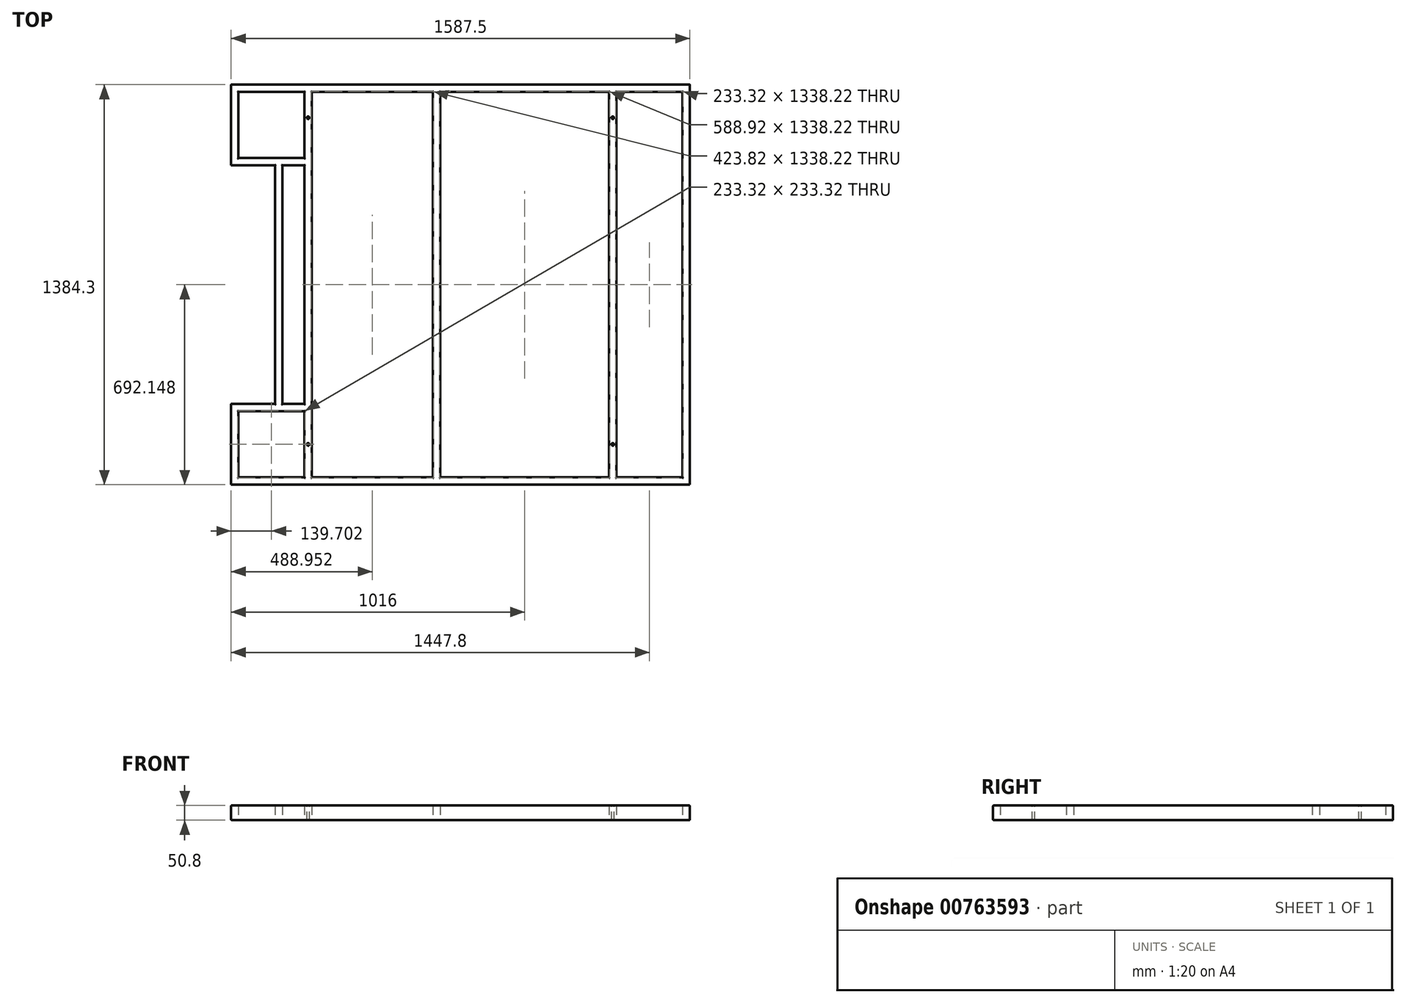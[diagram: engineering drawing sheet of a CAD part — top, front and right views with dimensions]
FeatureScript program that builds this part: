
annotation { "Feature Type Name" : "Feature", "Feature Type Description" : "" }
export const myFeature = defineFeature(function(context is Context, id is Id, definition is map)
    precondition{}
    {
        {
            var Q0;
            Q0=qCreatedBy(makeId("Top.planeOp"),FACE);
            var sketch = newSketch(context, id + "F0", { "sketchPlane" : qUnion([Q0])});
            skLineSegment(sketch, "E0", {"start": v(-927.94, -698.73) * mm, "end": v(659.56, -698.73) * mm});
            skLineSegment(sketch, "E1", {"start": v(659.56, -698.73) * mm, "end": v(659.56, 685.57) * mm});
            skLineSegment(sketch, "E2", {"start": v(659.56, 685.57) * mm, "end": v(-927.94, 685.57) * mm});
            skLineSegment(sketch, "E3", {"start": v(-927.94, 685.57) * mm, "end": v(-927.94, 406.17) * mm});
            skLineSegment(sketch, "E4", {"start": v(-673.94, 660.17) * mm, "end": v(-673.94, 431.57) * mm});
            skLineSegment(sketch, "E5", {"start": v(-927.94, -419.33) * mm, "end": v(-927.94, -698.73) * mm});
            skLineSegment(sketch, "E6", {"start": v(659.56, -6.58) * mm, "end": v(-673.94, -6.58) * mm, "construction": true});
            skLineSegment(sketch, "E7", {"start": v(-927.94, -419.33) * mm, "end": v(-775.54, -419.33) * mm});
            skLineSegment(sketch, "E8", {"start": v(-927.94, 406.17) * mm, "end": v(-775.54, 406.17) * mm});
            skLineSegment(sketch, "E9", {"start": v(-775.54, 406.17) * mm, "end": v(-775.54, -419.33) * mm});
            skLineSegment(sketch, "E10", {"start": v(380.16, 660.17) * mm, "end": v(380.16, -673.33) * mm});
            skLineSegment(sketch, "E11", {"start": v(-229.44, 660.17) * mm, "end": v(-229.44, -673.33) * mm});
            skLineSegment(sketch, "E12.0", {"start": v(634.16, 660.17) * mm, "end": v(405.56, 660.17) * mm});
            skLineSegment(sketch, "E13.0", {"start": v(-902.54, 660.17) * mm, "end": v(-902.54, 431.57) * mm});
            skLineSegment(sketch, "E14.0", {"start": v(-902.54, 431.57) * mm, "end": v(-673.94, 431.57) * mm});
            skLineSegment(sketch, "E15.0", {"start": v(-204.04, 660.17) * mm, "end": v(-204.04, -673.33) * mm});
            skLineSegment(sketch, "E16.trimOffspring", {"start": v(-229.44, 660.17) * mm, "end": v(-648.54, 660.17) * mm});
            skLineSegment(sketch, "E17.0", {"start": v(405.56, 660.17) * mm, "end": v(405.56, -673.33) * mm});
            skLineSegment(sketch, "E18.trimOffspring", {"start": v(380.16, 660.17) * mm, "end": v(-204.04, 660.17) * mm});
            skLineSegment(sketch, "E19.0", {"start": v(634.16, -673.33) * mm, "end": v(634.16, 660.17) * mm});
            skLineSegment(sketch, "E20.0", {"start": v(-648.54, 660.17) * mm, "end": v(-648.54, -673.33) * mm});
            skLineSegment(sketch, "E21.trimOffspring", {"start": v(-673.94, 660.17) * mm, "end": v(-902.54, 660.17) * mm});
            skLineSegment(sketch, "E22.trimOffspring", {"start": v(-673.94, 406.17) * mm, "end": v(-673.94, -419.33) * mm});
            skLineSegment(sketch, "E23.0", {"start": v(-750.14, 406.17) * mm, "end": v(-750.14, -419.33) * mm});
            skLineSegment(sketch, "E24.trimOffspring", {"start": v(-750.14, 406.17) * mm, "end": v(-673.94, 406.17) * mm});
            skLineSegment(sketch, "E25.0", {"start": v(-902.54, -673.33) * mm, "end": v(-673.94, -673.33) * mm});
            skLineSegment(sketch, "E26.trimOffspring", {"start": v(405.56, -673.33) * mm, "end": v(634.16, -673.33) * mm});
            skLineSegment(sketch, "E27.trimOffspring", {"start": v(-204.04, -673.33) * mm, "end": v(380.16, -673.33) * mm});
            skLineSegment(sketch, "E28.trimOffspring", {"start": v(-648.54, -673.33) * mm, "end": v(-229.44, -673.33) * mm});
            skLineSegment(sketch, "E29.trimOffspring", {"start": v(-750.14, -419.33) * mm, "end": v(-673.94, -419.33) * mm});
            skLineSegment(sketch, "E30.0", {"start": v(-902.54, -444.73) * mm, "end": v(-902.54, -673.33) * mm});
            skLineSegment(sketch, "E31.0", {"start": v(-902.54, -444.73) * mm, "end": v(-673.94, -444.73) * mm});
            skLineSegment(sketch, "E32.trimOffspring", {"start": v(-673.94, -444.73) * mm, "end": v(-673.94, -673.33) * mm});
            skSolve(sketch);
        }
        {
            var Q0;
            Q0 = qSketchRegion(id + "F0", true);
            extrude(context, id + "F1", {"entities" : qUnion([Q0]), "depth" : 50.8 * mm, "offsetDistance" : 25.4 * mm, "symmetric" : true});
        }
        {
            var Q0;
            Q0=makeQuery(id+"F1.opExtrude","CAP_EDGE",EDGE,{"disambiguationData":[OSD([sQuery(id+"F0.wireOp",EDGE,"E3")])],"isStart":false});
            var Q1;
            Q1=makeQuery(id+"F1.opExtrude","CAP_EDGE",EDGE,{"disambiguationData":[OSD([sQuery(id+"F0.wireOp",EDGE,"E8")])],"isStart":false});
            var Q2;
            Q2=makeQuery(id+"F1.opExtrude","CAP_EDGE",EDGE,{"disambiguationData":[OSD([sQuery(id+"F0.wireOp",EDGE,"E9")])],"isStart":false});
            var Q3;
            Q3=makeQuery(id+"F1.opExtrude","CAP_EDGE",EDGE,{"disambiguationData":[OSD([sQuery(id+"F0.wireOp",EDGE,"E2")])],"isStart":false});
            var Q4;
            Q4=makeQuery(id+"F1.opExtrude","CAP_EDGE",EDGE,{"disambiguationData":[OSD([sQuery(id+"F0.wireOp",EDGE,"E1")])],"isStart":false});
            var Q5;
            Q5=makeQuery(id+"F1.opExtrude","CAP_EDGE",EDGE,{"disambiguationData":[OSD([sQuery(id+"F0.wireOp",EDGE,"E0")])],"isStart":false});
            var Q6;
            Q6=makeQuery(id+"F1.opExtrude","CAP_EDGE",EDGE,{"disambiguationData":[OSD([sQuery(id+"F0.wireOp",EDGE,"E5")])],"isStart":false});
            var Q7;
            Q7=makeQuery(id+"F1.opExtrude","CAP_EDGE",EDGE,{"disambiguationData":[OSD([sQuery(id+"F0.wireOp",EDGE,"E7")])],"isStart":false});
            var Q8;
            Q8=makeQuery(id+"F1.opExtrude","CAP_EDGE",EDGE,{"disambiguationData":[OSD([sQuery(id+"F0.wireOp",EDGE,"E29.trimOffspring")])],"isStart":false});
            var Q9;
            Q9=makeQuery(id+"F1.opExtrude","CAP_EDGE",EDGE,{"disambiguationData":[OSD([sQuery(id+"F0.wireOp",EDGE,"E23.0")])],"isStart":false});
            var Q10;
            Q10=makeQuery(id+"F1.opExtrude","CAP_EDGE",EDGE,{"disambiguationData":[OSD([sQuery(id+"F0.wireOp",EDGE,"E31.0")])],"isStart":false});
            var Q11;
            Q11=makeQuery(id+"F1.opExtrude","CAP_EDGE",EDGE,{"disambiguationData":[OSD([sQuery(id+"F0.wireOp",EDGE,"E32.trimOffspring")])],"isStart":false});
            var Q12;
            Q12=makeQuery(id+"F1.opExtrude","CAP_EDGE",EDGE,{"disambiguationData":[OSD([sQuery(id+"F0.wireOp",EDGE,"E30.0")])],"isStart":false});
            var Q13;
            Q13=makeQuery(id+"F1.opExtrude","CAP_EDGE",EDGE,{"disambiguationData":[OSD([sQuery(id+"F0.wireOp",EDGE,"E25.0")])],"isStart":false});
            var Q14;
            Q14=makeQuery(id+"F1.opExtrude","CAP_EDGE",EDGE,{"disambiguationData":[OSD([sQuery(id+"F0.wireOp",EDGE,"E28.trimOffspring")])],"isStart":false});
            var Q15;
            Q15=makeQuery(id+"F1.opExtrude","CAP_EDGE",EDGE,{"disambiguationData":[OSD([sQuery(id+"F0.wireOp",EDGE,"E20.0")])],"isStart":false});
            var Q16;
            Q16=makeQuery(id+"F1.opExtrude","CAP_EDGE",EDGE,{"disambiguationData":[OSD([sQuery(id+"F0.wireOp",EDGE,"E11")])],"isStart":false});
            var Q17;
            Q17=makeQuery(id+"F1.opExtrude","CAP_EDGE",EDGE,{"disambiguationData":[OSD([sQuery(id+"F0.wireOp",EDGE,"E27.trimOffspring")])],"isStart":false});
            var Q18;
            Q18=makeQuery(id+"F1.opExtrude","CAP_EDGE",EDGE,{"disambiguationData":[OSD([sQuery(id+"F0.wireOp",EDGE,"E10")])],"isStart":false});
            var Q19;
            Q19=makeQuery(id+"F1.opExtrude","CAP_EDGE",EDGE,{"disambiguationData":[OSD([sQuery(id+"F0.wireOp",EDGE,"E26.trimOffspring")])],"isStart":false});
            var Q20;
            Q20=makeQuery(id+"F1.opExtrude","CAP_EDGE",EDGE,{"disambiguationData":[OSD([sQuery(id+"F0.wireOp",EDGE,"E19.0")])],"isStart":false});
            var Q21;
            Q21=makeQuery(id+"F1.opExtrude","CAP_EDGE",EDGE,{"disambiguationData":[OSD([sQuery(id+"F0.wireOp",EDGE,"E15.0")])],"isStart":false});
            var Q22;
            Q22=makeQuery(id+"F1.opExtrude","CAP_EDGE",EDGE,{"disambiguationData":[OSD([sQuery(id+"F0.wireOp",EDGE,"E17.0")])],"isStart":false});
            var Q23;
            Q23=makeQuery(id+"F1.opExtrude","CAP_EDGE",EDGE,{"disambiguationData":[OSD([sQuery(id+"F0.wireOp",EDGE,"E13.0")])],"isStart":false});
            var Q24;
            Q24=makeQuery(id+"F1.opExtrude","CAP_EDGE",EDGE,{"disambiguationData":[OSD([sQuery(id+"F0.wireOp",EDGE,"E14.0")])],"isStart":false});
            var Q25;
            Q25=makeQuery(id+"F1.opExtrude","CAP_EDGE",EDGE,{"disambiguationData":[OSD([sQuery(id+"F0.wireOp",EDGE,"E21.trimOffspring")])],"isStart":false});
            var Q26;
            Q26=makeQuery(id+"F1.opExtrude","CAP_EDGE",EDGE,{"disambiguationData":[OSD([sQuery(id+"F0.wireOp",EDGE,"E16.trimOffspring")])],"isStart":false});
            var Q27;
            Q27=makeQuery(id+"F1.opExtrude","CAP_EDGE",EDGE,{"disambiguationData":[OSD([sQuery(id+"F0.wireOp",EDGE,"E24.trimOffspring")])],"isStart":false});
            var Q28;
            Q28=makeQuery(id+"F1.opExtrude","CAP_EDGE",EDGE,{"disambiguationData":[OSD([sQuery(id+"F0.wireOp",EDGE,"E22.trimOffspring")])],"isStart":false});
            var Q29;
            Q29=makeQuery(id+"F1.opExtrude","CAP_EDGE",EDGE,{"disambiguationData":[OSD([sQuery(id+"F0.wireOp",EDGE,"E4")])],"isStart":false});
            var Q30;
            Q30=makeQuery(id+"F1.opExtrude","CAP_EDGE",EDGE,{"disambiguationData":[OSD([sQuery(id+"F0.wireOp",EDGE,"E18.trimOffspring")])],"isStart":false});
            var Q31;
            Q31=makeQuery(id+"F1.opExtrude","CAP_EDGE",EDGE,{"disambiguationData":[OSD([sQuery(id+"F0.wireOp",EDGE,"E12.0")])],"isStart":false});
            fillet(context, id + "F2", {"entities" : qUnion([Q0, Q1, Q2, Q3, Q4, Q5, Q6, Q7, Q8, Q9, Q10, Q11, Q12, Q13, Q14, Q15, Q16, Q17, Q18, Q19, Q20, Q21, Q22, Q23, Q24, Q25, Q26, Q27, Q28, Q29, Q30, Q31]), "radius" : 2.36 * mm, "tangentPropagation" : true, "allowEdgeOverflow" : false});
        }
        {
            var Q0;
            Q0=makeQuery(id+"F1.opExtrude","CAP_EDGE",EDGE,{"disambiguationData":[OSD([sQuery(id+"F0.wireOp",EDGE,"E5")])],"isStart":true});
            var Q1;
            Q1=makeQuery(id+"F1.opExtrude","CAP_EDGE",EDGE,{"disambiguationData":[OSD([sQuery(id+"F0.wireOp",EDGE,"E7")])],"isStart":true});
            var Q2;
            Q2=makeQuery(id+"F1.opExtrude","CAP_EDGE",EDGE,{"disambiguationData":[OSD([sQuery(id+"F0.wireOp",EDGE,"E30.0")])],"isStart":true});
            var Q3;
            Q3=makeQuery(id+"F1.opExtrude","CAP_EDGE",EDGE,{"disambiguationData":[OSD([sQuery(id+"F0.wireOp",EDGE,"E32.trimOffspring")])],"isStart":true});
            var Q4;
            Q4=makeQuery(id+"F1.opExtrude","CAP_EDGE",EDGE,{"disambiguationData":[OSD([sQuery(id+"F0.wireOp",EDGE,"E25.0")])],"isStart":true});
            var Q5;
            Q5=makeQuery(id+"F1.opExtrude","CAP_EDGE",EDGE,{"disambiguationData":[OSD([sQuery(id+"F0.wireOp",EDGE,"E0")])],"isStart":true});
            var Q6;
            Q6=makeQuery(id+"F1.opExtrude","CAP_EDGE",EDGE,{"disambiguationData":[OSD([sQuery(id+"F0.wireOp",EDGE,"E28.trimOffspring")])],"isStart":true});
            var Q7;
            Q7=makeQuery(id+"F1.opExtrude","CAP_EDGE",EDGE,{"disambiguationData":[OSD([sQuery(id+"F0.wireOp",EDGE,"E20.0")])],"isStart":true});
            var Q8;
            Q8=makeQuery(id+"F1.opExtrude","CAP_EDGE",EDGE,{"disambiguationData":[OSD([sQuery(id+"F0.wireOp",EDGE,"E11")])],"isStart":true});
            var Q9;
            Q9=makeQuery(id+"F1.opExtrude","CAP_EDGE",EDGE,{"disambiguationData":[OSD([sQuery(id+"F0.wireOp",EDGE,"E15.0")])],"isStart":true});
            var Q10;
            Q10=makeQuery(id+"F1.opExtrude","CAP_EDGE",EDGE,{"disambiguationData":[OSD([sQuery(id+"F0.wireOp",EDGE,"E31.0")])],"isStart":true});
            var Q11;
            Q11=makeQuery(id+"F1.opExtrude","CAP_EDGE",EDGE,{"disambiguationData":[OSD([sQuery(id+"F0.wireOp",EDGE,"E27.trimOffspring")])],"isStart":true});
            var Q12;
            Q12=makeQuery(id+"F1.opExtrude","CAP_EDGE",EDGE,{"disambiguationData":[OSD([sQuery(id+"F0.wireOp",EDGE,"E10")])],"isStart":true});
            var Q13;
            Q13=makeQuery(id+"F1.opExtrude","CAP_EDGE",EDGE,{"disambiguationData":[OSD([sQuery(id+"F0.wireOp",EDGE,"E17.0")])],"isStart":true});
            var Q14;
            Q14=makeQuery(id+"F1.opExtrude","CAP_EDGE",EDGE,{"disambiguationData":[OSD([sQuery(id+"F0.wireOp",EDGE,"E26.trimOffspring")])],"isStart":true});
            var Q15;
            Q15=makeQuery(id+"F1.opExtrude","CAP_EDGE",EDGE,{"disambiguationData":[OSD([sQuery(id+"F0.wireOp",EDGE,"E19.0")])],"isStart":true});
            var Q16;
            Q16=makeQuery(id+"F1.opExtrude","CAP_EDGE",EDGE,{"disambiguationData":[OSD([sQuery(id+"F0.wireOp",EDGE,"E12.0")])],"isStart":true});
            var Q17;
            Q17=makeQuery(id+"F1.opExtrude","CAP_EDGE",EDGE,{"disambiguationData":[OSD([sQuery(id+"F0.wireOp",EDGE,"E18.trimOffspring")])],"isStart":true});
            var Q18;
            Q18=makeQuery(id+"F1.opExtrude","CAP_EDGE",EDGE,{"disambiguationData":[OSD([sQuery(id+"F0.wireOp",EDGE,"E16.trimOffspring")])],"isStart":true});
            var Q19;
            Q19=makeQuery(id+"F1.opExtrude","CAP_EDGE",EDGE,{"disambiguationData":[OSD([sQuery(id+"F0.wireOp",EDGE,"E21.trimOffspring")])],"isStart":true});
            var Q20;
            Q20=makeQuery(id+"F1.opExtrude","CAP_EDGE",EDGE,{"disambiguationData":[OSD([sQuery(id+"F0.wireOp",EDGE,"E3")])],"isStart":true});
            var Q21;
            Q21=makeQuery(id+"F1.opExtrude","CAP_EDGE",EDGE,{"disambiguationData":[OSD([sQuery(id+"F0.wireOp",EDGE,"E8")])],"isStart":true});
            var Q22;
            Q22=makeQuery(id+"F1.opExtrude","CAP_EDGE",EDGE,{"disambiguationData":[OSD([sQuery(id+"F0.wireOp",EDGE,"E14.0")])],"isStart":true});
            var Q23;
            Q23=makeQuery(id+"F1.opExtrude","CAP_EDGE",EDGE,{"disambiguationData":[OSD([sQuery(id+"F0.wireOp",EDGE,"E4")])],"isStart":true});
            var Q24;
            Q24=makeQuery(id+"F1.opExtrude","CAP_EDGE",EDGE,{"disambiguationData":[OSD([sQuery(id+"F0.wireOp",EDGE,"E22.trimOffspring")])],"isStart":true});
            var Q25;
            Q25=makeQuery(id+"F1.opExtrude","CAP_EDGE",EDGE,{"disambiguationData":[OSD([sQuery(id+"F0.wireOp",EDGE,"E9")])],"isStart":true});
            var Q26;
            Q26=makeQuery(id+"F1.opExtrude","CAP_EDGE",EDGE,{"disambiguationData":[OSD([sQuery(id+"F0.wireOp",EDGE,"E23.0")])],"isStart":true});
            var Q27;
            Q27=makeQuery(id+"F1.opExtrude","CAP_EDGE",EDGE,{"disambiguationData":[OSD([sQuery(id+"F0.wireOp",EDGE,"E1")])],"isStart":true});
            var Q28;
            Q28=makeQuery(id+"F1.opExtrude","CAP_EDGE",EDGE,{"disambiguationData":[OSD([sQuery(id+"F0.wireOp",EDGE,"E29.trimOffspring")])],"isStart":true});
            var Q29;
            Q29=makeQuery(id+"F1.opExtrude","CAP_EDGE",EDGE,{"disambiguationData":[OSD([sQuery(id+"F0.wireOp",EDGE,"E2")])],"isStart":true});
            fillet(context, id + "F3", {"entities" : qUnion([Q0, Q1, Q2, Q3, Q4, Q5, Q6, Q7, Q8, Q9, Q10, Q11, Q12, Q13, Q14, Q15, Q16, Q17, Q18, Q19, Q20, Q21, Q22, Q23, Q24, Q25, Q26, Q27, Q28, Q29]), "radius" : 2.36 * mm, "tangentPropagation" : true, "allowEdgeOverflow" : false});
        }
        {
            var Q0;
            Q0=makeQuery(id+"F1.opExtrude","CAP_FACE",FACE,{"disambiguationData":[OSD([sQuery(id+"F0.wireOp",EDGE,"E0"),sQuery(id+"F0.wireOp",EDGE,"E1"),sQuery(id+"F0.wireOp",EDGE,"E2"),sQuery(id+"F0.wireOp",EDGE,"E3"),sQuery(id+"F0.wireOp",EDGE,"E4"),sQuery(id+"F0.wireOp",EDGE,"E5"),sQuery(id+"F0.wireOp",EDGE,"E7"),sQuery(id+"F0.wireOp",EDGE,"E8"),sQuery(id+"F0.wireOp",EDGE,"E9"),sQuery(id+"F0.wireOp",EDGE,"E10"),sQuery(id+"F0.wireOp",EDGE,"E11"),sQuery(id+"F0.wireOp",EDGE,"E12.0"),sQuery(id+"F0.wireOp",EDGE,"E13.0"),sQuery(id+"F0.wireOp",EDGE,"E14.0"),sQuery(id+"F0.wireOp",EDGE,"E15.0"),sQuery(id+"F0.wireOp",EDGE,"E16.trimOffspring"),sQuery(id+"F0.wireOp",EDGE,"E17.0"),sQuery(id+"F0.wireOp",EDGE,"E18.trimOffspring"),sQuery(id+"F0.wireOp",EDGE,"E19.0"),sQuery(id+"F0.wireOp",EDGE,"E20.0"),sQuery(id+"F0.wireOp",EDGE,"E21.trimOffspring"),sQuery(id+"F0.wireOp",EDGE,"E22.trimOffspring"),sQuery(id+"F0.wireOp",EDGE,"E23.0"),sQuery(id+"F0.wireOp",EDGE,"E24.trimOffspring"),sQuery(id+"F0.wireOp",EDGE,"E25.0"),sQuery(id+"F0.wireOp",EDGE,"E26.trimOffspring"),sQuery(id+"F0.wireOp",EDGE,"E27.trimOffspring"),sQuery(id+"F0.wireOp",EDGE,"E28.trimOffspring"),sQuery(id+"F0.wireOp",EDGE,"E29.trimOffspring"),sQuery(id+"F0.wireOp",EDGE,"E30.0"),sQuery(id+"F0.wireOp",EDGE,"E31.0"),sQuery(id+"F0.wireOp",EDGE,"E32.trimOffspring")])],"isStart":true});
            var sketch = newSketch(context, id + "F4", { "sketchPlane" : qUnion([Q0])});
            skLineSegment(sketch, "E33", {"start": v(-661.24, 696.37) * mm, "end": v(-661.24, 559.03) * mm, "construction": true});
            skLineSegment(sketch, "E34", {"start": v(392.86, 698.73) * mm, "end": v(392.86, 559.03) * mm, "construction": true});
            skLineSegment(sketch, "E35", {"start": v(-661.24, -685.57) * mm, "end": v(-661.24, -571.27) * mm, "construction": true});
            skLineSegment(sketch, "E36", {"start": v(392.86, -685.57) * mm, "end": v(392.86, -571.27) * mm, "construction": true});
            skSolve(sketch);
        }
        {
            var Q0;
            Q0=sQuery(id+"F4.wireOp",VERTEX,"E35.end");
            var Q1;
            Q1=sQuery(id+"F4.wireOp",VERTEX,"E33.end");
            var Q2;
            Q2=sQuery(id+"F4.wireOp",VERTEX,"E34.end");
            var Q3;
            Q3=sQuery(id+"F4.wireOp",VERTEX,"E36.end");
            var Q4;
            Q4=makeQuery(id+"F1.opExtrude","SWEPT_BODY",BODY,{"disambiguationData":[OSD([sQuery(id+"F0.wireOp",EDGE,"E0"),sQuery(id+"F0.wireOp",EDGE,"E1"),sQuery(id+"F0.wireOp",EDGE,"E2"),sQuery(id+"F0.wireOp",EDGE,"E3"),sQuery(id+"F0.wireOp",EDGE,"E4"),sQuery(id+"F0.wireOp",EDGE,"E5"),sQuery(id+"F0.wireOp",EDGE,"E7"),sQuery(id+"F0.wireOp",EDGE,"E8"),sQuery(id+"F0.wireOp",EDGE,"E9"),sQuery(id+"F0.wireOp",EDGE,"E10"),sQuery(id+"F0.wireOp",EDGE,"E11"),sQuery(id+"F0.wireOp",EDGE,"E12.0"),sQuery(id+"F0.wireOp",EDGE,"E13.0"),sQuery(id+"F0.wireOp",EDGE,"E14.0"),sQuery(id+"F0.wireOp",EDGE,"E15.0"),sQuery(id+"F0.wireOp",EDGE,"E16.trimOffspring"),sQuery(id+"F0.wireOp",EDGE,"E17.0"),sQuery(id+"F0.wireOp",EDGE,"E18.trimOffspring"),sQuery(id+"F0.wireOp",EDGE,"E19.0"),sQuery(id+"F0.wireOp",EDGE,"E20.0"),sQuery(id+"F0.wireOp",EDGE,"E21.trimOffspring"),sQuery(id+"F0.wireOp",EDGE,"E22.trimOffspring"),sQuery(id+"F0.wireOp",EDGE,"E23.0"),sQuery(id+"F0.wireOp",EDGE,"E24.trimOffspring"),sQuery(id+"F0.wireOp",EDGE,"E25.0"),sQuery(id+"F0.wireOp",EDGE,"E26.trimOffspring"),sQuery(id+"F0.wireOp",EDGE,"E27.trimOffspring"),sQuery(id+"F0.wireOp",EDGE,"E28.trimOffspring"),sQuery(id+"F0.wireOp",EDGE,"E29.trimOffspring"),sQuery(id+"F0.wireOp",EDGE,"E30.0"),sQuery(id+"F0.wireOp",EDGE,"E31.0"),sQuery(id+"F0.wireOp",EDGE,"E32.trimOffspring")])]});
            hole(context, id + "F5", {"style" : HoleStyle.SIMPLE, "endStyle" : HoleEndStyle.THROUGH, "holeDiameter" : 8.73 * mm, "majorDiameter" : 6.35 * mm, "isTappedThrough" : true, "tappedDepth" : 12.7 * mm, "tapClearance" : 3, "locations" : qUnion([Q0, Q1, Q2, Q3]), "scope" : qUnion([Q4]), "startStyle" : HoleStartStyle.PART});
        }
    });
